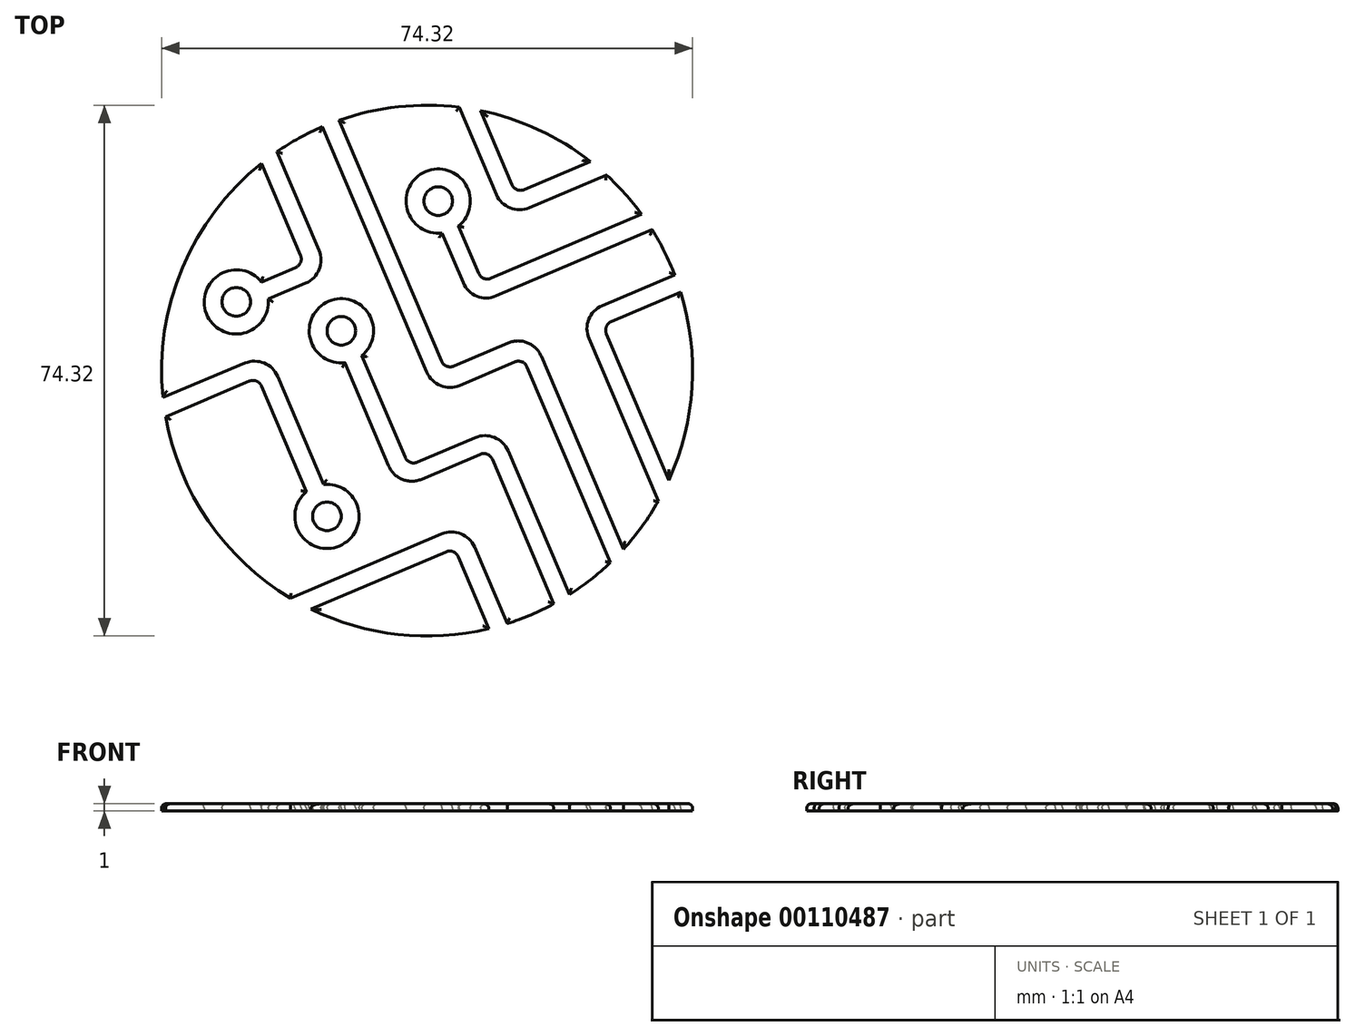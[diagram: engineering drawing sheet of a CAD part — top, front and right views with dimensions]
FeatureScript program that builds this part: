
annotation { "Feature Type Name" : "Feature", "Feature Type Description" : "" }
export const myFeature = defineFeature(function(context is Context, id is Id, definition is map)
    precondition{}
    {
        {
            var Q0;
            Q0=qCreatedBy(makeId("Top.planeOp"),FACE);
            var sketch = newSketch(context, id + "F0", { "sketchPlane" : qUnion([Q0])});
            skPoint(sketch, "E0", {"position": v(0, 42.25) * mm});
            skArc(sketch, "E1", {"start": v(-35.8, -3.78) * mm, "mid": v(-29.82, -18.38) * mm, "end": v(-18.32, -29.18) * mm});
            skLineSegment(sketch, "E2", {"start": v(-11.55, 37.74) * mm, "end": v(2.8, 4) * mm});
            skLineSegment(sketch, "E3", {"start": v(4.51, 3.31) * mm, "end": v(12.17, 6.57) * mm});
            skLineSegment(sketch, "E4", {"start": v(16.76, 4.72) * mm, "end": v(28.27, -22.33) * mm});
            skLineSegment(sketch, "E5", {"start": v(26.44, -24.2) * mm, "end": v(14.78, 3.22) * mm});
            skLineSegment(sketch, "E6", {"start": v(13.07, 3.9) * mm, "end": v(5.35, 0.62) * mm});
            skLineSegment(sketch, "E7", {"start": v(0.75, 2.47) * mm, "end": v(-13.87, 36.84) * mm});
            skLineSegment(sketch, "E8", {"start": v(-20.22, 33.34) * mm, "end": v(-14.35, 19.54) * mm});
            skLineSegment(sketch, "E9", {"start": v(-16.2, 14.94) * mm, "end": v(-21.43, 12.72) * mm});
            skLineSegment(sketch, "E10", {"start": v(-22.41, 31.72) * mm, "end": v(-16.93, 18.83) * mm});
            skLineSegment(sketch, "E11", {"start": v(-17.61, 17.12) * mm, "end": v(-22.38, 15.1) * mm});
            skLineSegment(sketch, "E12", {"start": v(32.27, 22.43) * mm, "end": v(10.44, 13.14) * mm});
            skLineSegment(sketch, "E13", {"start": v(5.84, 14.99) * mm, "end": v(2.88, 21.96) * mm});
            skLineSegment(sketch, "E14", {"start": v(5.2, 22.94) * mm, "end": v(8.01, 16.3) * mm});
            skLineSegment(sketch, "E15", {"start": v(9.72, 15.62) * mm, "end": v(30.8, 24.6) * mm});
            skLineSegment(sketch, "E16", {"start": v(35.45, 16.1) * mm, "end": v(25.3, 11.77) * mm});
            skLineSegment(sketch, "E17", {"start": v(23.45, 7.18) * mm, "end": v(33.14, -15.6) * mm});
            skLineSegment(sketch, "E18", {"start": v(34.63, -12.67) * mm, "end": v(25.9, 7.87) * mm});
            skLineSegment(sketch, "E19", {"start": v(26.58, 9.57) * mm, "end": v(36.28, 13.7) * mm});
            skLineSegment(sketch, "E20", {"start": v(5.3, 39.58) * mm, "end": v(10.5, 27.34) * mm});
            skLineSegment(sketch, "E21", {"start": v(15.1, 25.49) * mm, "end": v(25.9, 30.09) * mm});
            skLineSegment(sketch, "E22", {"start": v(8.26, 39.1) * mm, "end": v(12.68, 28.72) * mm});
            skLineSegment(sketch, "E23", {"start": v(14.38, 28.03) * mm, "end": v(23.66, 31.98) * mm});
            skLineSegment(sketch, "E24", {"start": v(-18.32, -29.18) * mm, "end": v(2.84, -20.18) * mm});
            skLineSegment(sketch, "E25", {"start": v(7.43, -22.03) * mm, "end": v(12, -32.75) * mm});
            skLineSegment(sketch, "E26", {"start": v(-15.46, -30.73) * mm, "end": v(3.43, -22.7) * mm});
            skLineSegment(sketch, "E27", {"start": v(5.14, -23.38) * mm, "end": v(9.43, -33.46) * mm});
            skLineSegment(sketch, "E28", {"start": v(20.7, -28.7) * mm, "end": v(12.12, -8.54) * mm});
            skLineSegment(sketch, "E29", {"start": v(7.53, -6.7) * mm, "end": v(-0.59, -10.15) * mm});
            skLineSegment(sketch, "E30", {"start": v(-2.3, -9.46) * mm, "end": v(-8.35, 4.78) * mm});
            skLineSegment(sketch, "E31", {"start": v(-10.69, 3.79) * mm, "end": v(-4.59, -10.67) * mm});
            skLineSegment(sketch, "E32", {"start": v(0, -12.52) * mm, "end": v(8.2, -9.04) * mm});
            skLineSegment(sketch, "E33", {"start": v(9.91, -9.72) * mm, "end": v(18.53, -29.97) * mm});
            skLineSegment(sketch, "E34", {"start": v(-35.8, -3.78) * mm, "end": v(-24.09, 1.21) * mm});
            skLineSegment(sketch, "E35", {"start": v(-22.38, 0.52) * mm, "end": v(-16.13, -14.28) * mm});
            skLineSegment(sketch, "E36", {"start": v(-13.68, -13.24) * mm, "end": v(-20.12, 1.87) * mm});
            skLineSegment(sketch, "E37", {"start": v(-24.68, 3.74) * mm, "end": v(-36.19, -1.03) * mm});
            skPoint(sketch, "E37.endSnap0", {"position": v(-29.35, -1.03) * mm});
            skPoint(sketch, "E38.visualSharp", {"position": v(-16.42, 17.63) * mm});
            skArc(sketch, "E38.filletArc", {"start": v(-17.61, 17.12) * mm, "mid": v(-16.92, 17.83) * mm, "end": v(-16.93, 18.83) * mm});
            skPoint(sketch, "E39.visualSharp", {"position": v(13.19, 27.52) * mm});
            skArc(sketch, "E39.filletArc", {"start": v(12.68, 28.72) * mm, "mid": v(13.39, 28.02) * mm, "end": v(14.38, 28.03) * mm});
            skPoint(sketch, "E40.visualSharp", {"position": v(25.38, 9.06) * mm});
            skArc(sketch, "E40.filletArc", {"start": v(26.58, 9.57) * mm, "mid": v(25.88, 8.86) * mm, "end": v(25.9, 7.87) * mm});
            skPoint(sketch, "E41.visualSharp", {"position": v(8.52, 15.1) * mm});
            skArc(sketch, "E41.filletArc", {"start": v(8.01, 16.3) * mm, "mid": v(8.73, 15.6) * mm, "end": v(9.72, 15.62) * mm});
            skPoint(sketch, "E42.visualSharp", {"position": v(14.27, 4.42) * mm});
            skArc(sketch, "E42.filletArc", {"start": v(14.78, 3.22) * mm, "mid": v(14.06, 3.92) * mm, "end": v(13.07, 3.9) * mm});
            skPoint(sketch, "E43.visualSharp", {"position": v(9.4, -8.53) * mm});
            skArc(sketch, "E43.filletArc", {"start": v(9.91, -9.72) * mm, "mid": v(9.2, -9.03) * mm, "end": v(8.2, -9.04) * mm});
            skPoint(sketch, "E44.visualSharp", {"position": v(4.63, -22.18) * mm});
            skArc(sketch, "E44.filletArc", {"start": v(5.14, -23.38) * mm, "mid": v(4.43, -22.68) * mm, "end": v(3.43, -22.7) * mm});
            skPoint(sketch, "E45.visualSharp", {"position": v(-1.78, -10.65) * mm});
            skArc(sketch, "E45.filletArc", {"start": v(-2.3, -9.46) * mm, "mid": v(-1.58, -10.16) * mm, "end": v(-0.59, -10.15) * mm});
            skPoint(sketch, "E46.visualSharp", {"position": v(3.32, 2.8) * mm});
            skArc(sketch, "E46.filletArc", {"start": v(2.8, 4) * mm, "mid": v(3.52, 3.3) * mm, "end": v(4.51, 3.31) * mm});
            skPoint(sketch, "E47.visualSharp", {"position": v(-22.89, 1.72) * mm});
            skArc(sketch, "E47.filletArc", {"start": v(-22.38, 0.52) * mm, "mid": v(-23.1, 1.22) * mm, "end": v(-24.09, 1.21) * mm});
            skPoint(sketch, "E48.visualSharp", {"position": v(6.06, -18.8) * mm});
            skArc(sketch, "E48.filletArc", {"start": v(7.43, -22.03) * mm, "mid": v(5.52, -20.15) * mm, "end": v(2.84, -20.18) * mm});
            skPoint(sketch, "E49.visualSharp", {"position": v(10.75, -5.32) * mm});
            skArc(sketch, "E49.filletArc", {"start": v(12.12, -8.54) * mm, "mid": v(10.2, -6.66) * mm, "end": v(7.53, -6.7) * mm});
            skPoint(sketch, "E50.visualSharp", {"position": v(-3.22, -13.9) * mm});
            skArc(sketch, "E50.filletArc", {"start": v(-4.59, -10.67) * mm, "mid": v(-2.67, -12.55) * mm, "end": v(0, -12.52) * mm});
            skPoint(sketch, "E51.visualSharp", {"position": v(2.12, -0.75) * mm});
            skArc(sketch, "E51.filletArc", {"start": v(0.75, 2.47) * mm, "mid": v(2.67, 0.6) * mm, "end": v(5.35, 0.62) * mm});
            skPoint(sketch, "E52.visualSharp", {"position": v(15.39, 7.94) * mm});
            skArc(sketch, "E52.filletArc", {"start": v(16.76, 4.72) * mm, "mid": v(14.85, 6.6) * mm, "end": v(12.17, 6.57) * mm});
            skPoint(sketch, "E53.visualSharp", {"position": v(22.08, 10.4) * mm});
            skArc(sketch, "E53.filletArc", {"start": v(25.3, 11.77) * mm, "mid": v(23.42, 9.86) * mm, "end": v(23.45, 7.18) * mm});
            skPoint(sketch, "E54.visualSharp", {"position": v(7.22, 11.77) * mm});
            skArc(sketch, "E54.filletArc", {"start": v(5.84, 14.99) * mm, "mid": v(7.76, 13.11) * mm, "end": v(10.44, 13.14) * mm});
            skPoint(sketch, "E55.visualSharp", {"position": v(11.87, 24.12) * mm});
            skArc(sketch, "E55.filletArc", {"start": v(10.5, 27.34) * mm, "mid": v(12.41, 25.46) * mm, "end": v(15.1, 25.49) * mm});
            skPoint(sketch, "E56.visualSharp", {"position": v(-12.98, 16.31) * mm});
            skArc(sketch, "E56.filletArc", {"start": v(-16.2, 14.94) * mm, "mid": v(-14.33, 16.86) * mm, "end": v(-14.35, 19.54) * mm});
            skPoint(sketch, "E57.visualSharp", {"position": v(-21.47, 5.06) * mm});
            skArc(sketch, "E57.filletArc", {"start": v(-20.12, 1.87) * mm, "mid": v(-22.01, 3.74) * mm, "end": v(-24.68, 3.74) * mm});
            skArc(sketch, "E58", {"start": v(5.2, 22.94) * mm, "mid": v(0.59, 30.57) * mm, "end": v(2.88, 21.96) * mm});
            skArc(sketch, "E59", {"start": v(-22.38, 15.1) * mm, "mid": v(-30.1, 10.65) * mm, "end": v(-21.43, 12.72) * mm});
            skArc(sketch, "E60", {"start": v(-8.35, 4.78) * mm, "mid": v(-12.97, 12.4) * mm, "end": v(-10.69, 3.79) * mm});
            skArc(sketch, "E61", {"start": v(-16.13, -14.28) * mm, "mid": v(-11.46, -21.86) * mm, "end": v(-13.68, -13.24) * mm});
            skCircle(sketch, "E62", {"center": v(-25.92, 12.31) * mm, "radius": 2 * mm});
            skCircle(sketch, "E63", {"center": v(2.35, 26.42) * mm, "radius": 2 * mm});
            skCircle(sketch, "E64", {"center": v(-11.21, 8.26) * mm, "radius": 2 * mm});
            skCircle(sketch, "E65", {"center": v(-13.22, -17.72) * mm, "radius": 2 * mm});
            skArc(sketch, "E66.trimOffspring", {"start": v(23.66, 31.98) * mm, "mid": v(16.37, 36.42) * mm, "end": v(8.26, 39.1) * mm});
            skArc(sketch, "E67.trimOffspring", {"start": v(-13.87, 36.84) * mm, "mid": v(-17.13, 35.24) * mm, "end": v(-20.22, 33.34) * mm});
            skArc(sketch, "E68.trimOffspring", {"start": v(5.3, 39.58) * mm, "mid": v(-3.24, 39.63) * mm, "end": v(-11.55, 37.74) * mm});
            skArc(sketch, "E69.trimOffspring", {"start": v(30.8, 24.6) * mm, "mid": v(28.49, 27.46) * mm, "end": v(25.9, 30.09) * mm});
            skArc(sketch, "E70.trimOffspring", {"start": v(35.45, 16.1) * mm, "mid": v(34.01, 19.34) * mm, "end": v(32.27, 22.43) * mm});
            skArc(sketch, "E71.trimOffspring", {"start": v(34.63, -12.67) * mm, "mid": v(37.88, 0.36) * mm, "end": v(36.28, 13.7) * mm});
            skArc(sketch, "E72.trimOffspring", {"start": v(28.27, -22.33) * mm, "mid": v(30.9, -19.1) * mm, "end": v(33.14, -15.6) * mm});
            skArc(sketch, "E73.trimOffspring", {"start": v(20.7, -28.7) * mm, "mid": v(23.68, -26.59) * mm, "end": v(26.44, -24.2) * mm});
            skArc(sketch, "E74.trimOffspring", {"start": v(12, -32.75) * mm, "mid": v(15.33, -31.51) * mm, "end": v(18.53, -29.97) * mm});
            skArc(sketch, "E75.trimOffspring", {"start": v(-15.46, -30.73) * mm, "mid": v(-3.25, -34.25) * mm, "end": v(9.43, -33.46) * mm});
            skArc(sketch, "E76.trimOffspring", {"start": v(-22.41, 31.72) * mm, "mid": v(-33.46, 17.1) * mm, "end": v(-36.19, -1.03) * mm});
            skSolve(sketch);
        }
        {
            var Q0;
            Q0 = qSketchRegion(id + "F0", true);
            extrude(context, id + "F1", {"entities" : qUnion([Q0]), "depth" : 1 * mm});
        }
        {
            var Q0;
            Q0=makeQuery(id+"F1.opExtrude","CAP_FACE",FACE,{"disambiguationData":[OSD([sQuery(id+"F0.wireOp",EDGE,"E1"),sQuery(id+"F0.wireOp",EDGE,"E5"),sQuery(id+"F0.wireOp",EDGE,"E6"),sQuery(id+"F0.wireOp",EDGE,"E7"),sQuery(id+"F0.wireOp",EDGE,"E8"),sQuery(id+"F0.wireOp",EDGE,"E9"),sQuery(id+"F0.wireOp",EDGE,"E10"),sQuery(id+"F0.wireOp",EDGE,"E11"),sQuery(id+"F0.wireOp",EDGE,"E24"),sQuery(id+"F0.wireOp",EDGE,"E25"),sQuery(id+"F0.wireOp",EDGE,"E28"),sQuery(id+"F0.wireOp",EDGE,"E29"),sQuery(id+"F0.wireOp",EDGE,"E30"),sQuery(id+"F0.wireOp",EDGE,"E31"),sQuery(id+"F0.wireOp",EDGE,"E32"),sQuery(id+"F0.wireOp",EDGE,"E33"),sQuery(id+"F0.wireOp",EDGE,"E34"),sQuery(id+"F0.wireOp",EDGE,"E35"),sQuery(id+"F0.wireOp",EDGE,"E36"),sQuery(id+"F0.wireOp",EDGE,"E37"),sQuery(id+"F0.wireOp",EDGE,"E38.filletArc"),sQuery(id+"F0.wireOp",EDGE,"E42.filletArc"),sQuery(id+"F0.wireOp",EDGE,"E43.filletArc"),sQuery(id+"F0.wireOp",EDGE,"E45.filletArc"),sQuery(id+"F0.wireOp",EDGE,"E47.filletArc"),sQuery(id+"F0.wireOp",EDGE,"E48.filletArc"),sQuery(id+"F0.wireOp",EDGE,"E49.filletArc"),sQuery(id+"F0.wireOp",EDGE,"E50.filletArc"),sQuery(id+"F0.wireOp",EDGE,"E51.filletArc"),sQuery(id+"F0.wireOp",EDGE,"E56.filletArc"),sQuery(id+"F0.wireOp",EDGE,"E57.filletArc"),sQuery(id+"F0.wireOp",EDGE,"E59"),sQuery(id+"F0.wireOp",EDGE,"E60"),sQuery(id+"F0.wireOp",EDGE,"E61"),sQuery(id+"F0.wireOp",EDGE,"E67.trimOffspring"),sQuery(id+"F0.wireOp",EDGE,"E73.trimOffspring"),sQuery(id+"F0.wireOp",EDGE,"E74.trimOffspring"),sQuery(id+"F0.wireOp",EDGE,"E76.trimOffspring")])],"isStart":false});
            var Q1;
            Q1=makeQuery(id+"F1.opExtrude","CAP_FACE",FACE,{"disambiguationData":[OSD([sQuery(id+"F0.wireOp",EDGE,"E2"),sQuery(id+"F0.wireOp",EDGE,"E3"),sQuery(id+"F0.wireOp",EDGE,"E4"),sQuery(id+"F0.wireOp",EDGE,"E12"),sQuery(id+"F0.wireOp",EDGE,"E13"),sQuery(id+"F0.wireOp",EDGE,"E14"),sQuery(id+"F0.wireOp",EDGE,"E15"),sQuery(id+"F0.wireOp",EDGE,"E16"),sQuery(id+"F0.wireOp",EDGE,"E17"),sQuery(id+"F0.wireOp",EDGE,"E20"),sQuery(id+"F0.wireOp",EDGE,"E21"),sQuery(id+"F0.wireOp",EDGE,"E41.filletArc"),sQuery(id+"F0.wireOp",EDGE,"E46.filletArc"),sQuery(id+"F0.wireOp",EDGE,"E52.filletArc"),sQuery(id+"F0.wireOp",EDGE,"E53.filletArc"),sQuery(id+"F0.wireOp",EDGE,"E54.filletArc"),sQuery(id+"F0.wireOp",EDGE,"E55.filletArc"),sQuery(id+"F0.wireOp",EDGE,"E58"),sQuery(id+"F0.wireOp",EDGE,"E68.trimOffspring"),sQuery(id+"F0.wireOp",EDGE,"E69.trimOffspring"),sQuery(id+"F0.wireOp",EDGE,"E70.trimOffspring"),sQuery(id+"F0.wireOp",EDGE,"E72.trimOffspring")])],"isStart":false});
            var Q2;
            Q2=makeQuery(id+"F1.opExtrude","CAP_FACE",FACE,{"disambiguationData":[OSD([sQuery(id+"F0.wireOp",EDGE,"E22"),sQuery(id+"F0.wireOp",EDGE,"E23"),sQuery(id+"F0.wireOp",EDGE,"E39.filletArc"),sQuery(id+"F0.wireOp",EDGE,"E66.trimOffspring")])],"isStart":false});
            var Q3;
            Q3=makeQuery(id+"F1.opExtrude","CAP_FACE",FACE,{"disambiguationData":[OSD([sQuery(id+"F0.wireOp",EDGE,"E18"),sQuery(id+"F0.wireOp",EDGE,"E19"),sQuery(id+"F0.wireOp",EDGE,"E40.filletArc"),sQuery(id+"F0.wireOp",EDGE,"E71.trimOffspring")])],"isStart":false});
            var Q4;
            Q4=makeQuery(id+"F1.opExtrude","CAP_FACE",FACE,{"disambiguationData":[OSD([sQuery(id+"F0.wireOp",EDGE,"E26"),sQuery(id+"F0.wireOp",EDGE,"E27"),sQuery(id+"F0.wireOp",EDGE,"E44.filletArc"),sQuery(id+"F0.wireOp",EDGE,"E75.trimOffspring")])],"isStart":false});
            var Q5;
            Q5=makeQuery(id+"F1.opExtrude","CAP_FACE",FACE,{"disambiguationData":[OSD([sQuery(id+"F0.wireOp",EDGE,"E63")])],"isStart":false});
            var Q6;
            Q6=makeQuery(id+"F1.opExtrude","CAP_FACE",FACE,{"disambiguationData":[OSD([sQuery(id+"F0.wireOp",EDGE,"E64")])],"isStart":false});
            var Q7;
            Q7=makeQuery(id+"F1.opExtrude","CAP_FACE",FACE,{"disambiguationData":[OSD([sQuery(id+"F0.wireOp",EDGE,"E65")])],"isStart":false});
            var Q8;
            Q8=makeQuery(id+"F1.opExtrude","CAP_FACE",FACE,{"disambiguationData":[OSD([sQuery(id+"F0.wireOp",EDGE,"E62")])],"isStart":false});
            fillet(context, id + "F2", {"entities" : qUnion([Q0, Q1, Q2, Q3, Q4, Q5, Q6, Q7, Q8]), "radius" : .6 * mm, "tangentPropagation" : true, "allowEdgeOverflow" : false});
        }
    });
